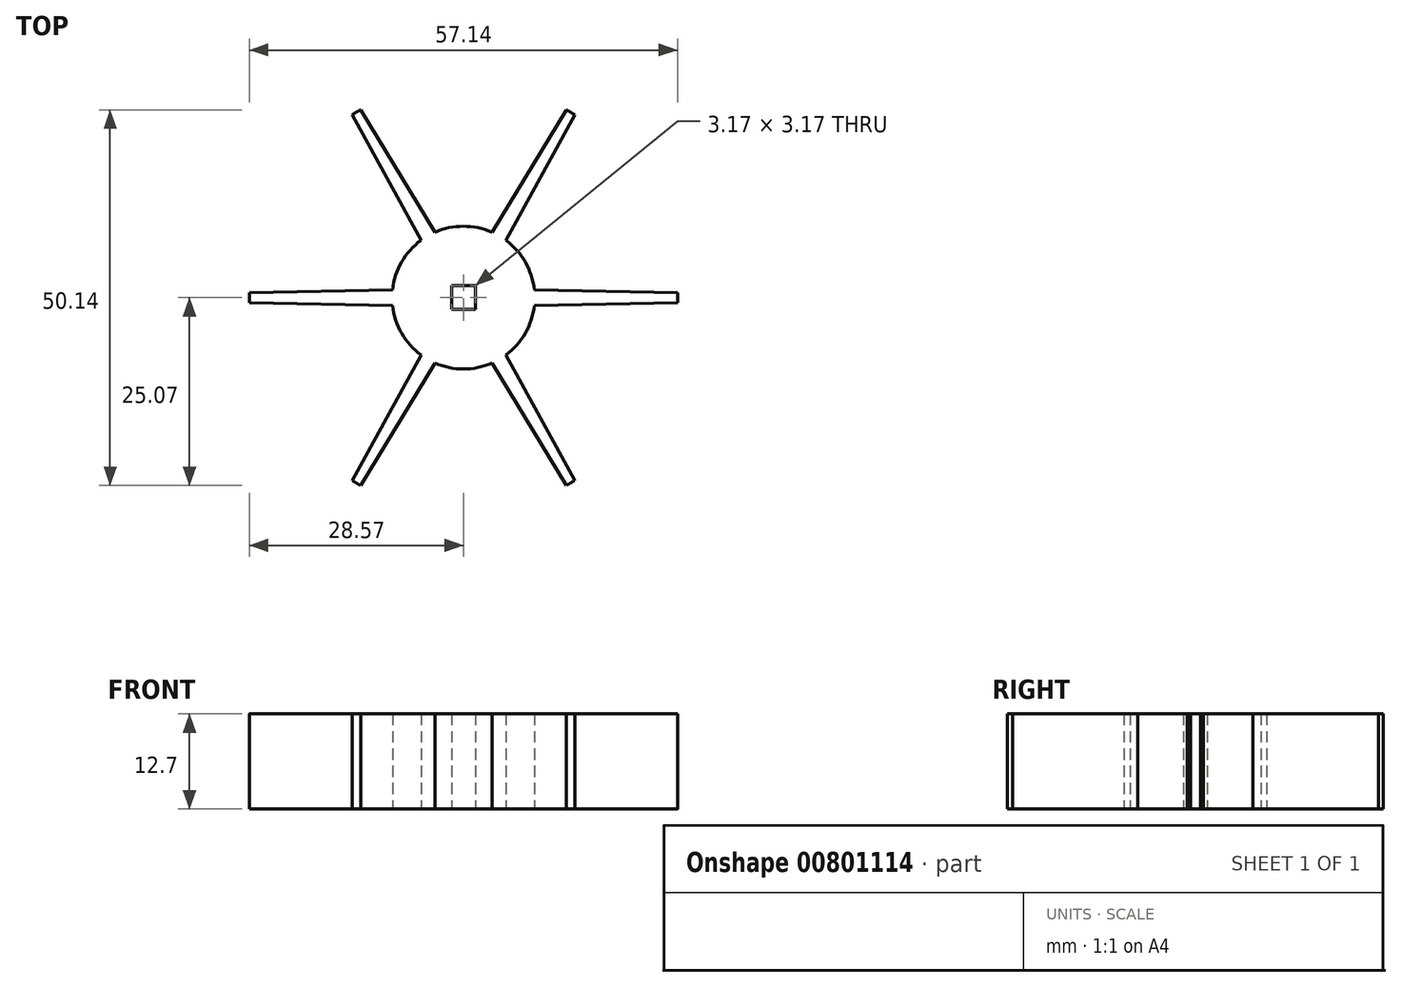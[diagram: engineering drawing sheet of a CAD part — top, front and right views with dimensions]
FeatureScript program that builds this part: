
annotation { "Feature Type Name" : "Feature", "Feature Type Description" : "" }
export const myFeature = defineFeature(function(context is Context, id is Id, definition is map)
    precondition{}
    {
        {
            var Q0;
            Q0=qCreatedBy(makeId("Top.planeOp"),FACE);
            var sketch = newSketch(context, id + "F0", { "sketchPlane" : qUnion([Q0])});
            skCircle(sketch, "E0", {"center": v(0, 0) * mm, "radius": 28.58 * mm});
            skCircle(sketch, "E1", {"center": v(0, 0) * mm, "radius": 9.53 * mm});
            skLineSegment(sketch, "E2", {"start": v(0, 0) * mm, "end": v(0, -28.58) * mm, "construction": true});
            skLineSegment(sketch, "E3", {"start": v(-3.8, -8.73) * mm, "end": v(-13.72, -25.07) * mm});
            skLineSegment(sketch, "E4.MirrorCS", {"start": v(3.81, -8.73) * mm, "end": v(13.72, -25.07) * mm});
            skLineSegment(sketch, "E5.1.1", {"start": v(9.47, -1.07) * mm, "end": v(28.57, -0.66) * mm});
            skLineSegment(sketch, "E5.1.2", {"start": v(5.66, -7.66) * mm, "end": v(14.85, -24.41) * mm});
            skLineSegment(sketch, "E5.2.1", {"start": v(5.66, 7.66) * mm, "end": v(14.85, 24.41) * mm});
            skLineSegment(sketch, "E5.2.2", {"start": v(9.47, 1.07) * mm, "end": v(28.57, 0.66) * mm});
            skLineSegment(sketch, "E5.3.1", {"start": v(-3.8, 8.73) * mm, "end": v(-13.72, 25.07) * mm});
            skLineSegment(sketch, "E5.3.2", {"start": v(3.81, 8.73) * mm, "end": v(13.72, 25.07) * mm});
            skLineSegment(sketch, "E5.4.1", {"start": v(-9.47, 1.07) * mm, "end": v(-28.57, 0.66) * mm});
            skLineSegment(sketch, "E5.4.2", {"start": v(-5.66, 7.66) * mm, "end": v(-14.85, 24.41) * mm});
            skLineSegment(sketch, "E5.5.1", {"start": v(-5.66, -7.66) * mm, "end": v(-14.85, -24.41) * mm});
            skLineSegment(sketch, "E5.5.2", {"start": v(-9.47, -1.07) * mm, "end": v(-28.57, -0.66) * mm});
            skLineSegment(sketch, "E6.bottom", {"start": v(1.59, 1.59) * mm, "end": v(-1.59, 1.59) * mm});
            skLineSegment(sketch, "E6.top", {"start": v(1.59, -1.59) * mm, "end": v(-1.59, -1.59) * mm});
            skLineSegment(sketch, "E6.left", {"start": v(1.59, 1.59) * mm, "end": v(1.59, -1.59) * mm});
            skLineSegment(sketch, "E6.right", {"start": v(-1.59, 1.59) * mm, "end": v(-1.59, -1.59) * mm});
            skSolve(sketch);
        }
        {
            var Q0;
            Q0=makeQuery(id+"F0.imprint","IMPRINT",FACE,{"disambiguationData":[TD([[makeQuery(id+"F0.imprint","IMPRINT",EDGE,{"derivedFrom":sQuery(id+"F0.wireOp",EDGE,"E6.bottom")}),-1.0]])]});
            var Q1;
            {var subQ0=sQuery(id+"F0.wireOp",EDGE,"E5.4.1");Q1=makeQuery(id+"F0.imprint","IMPRINT",FACE,{"disambiguationData":[TD([[makeQuery(id+"F0.imprint","IMPRINT",EDGE,{"derivedFrom":subQ0}),1.0]])]});}
            var Q2;
            {var subQ0=sQuery(id+"F0.wireOp",EDGE,"E5.3.1");Q2=makeQuery(id+"F0.imprint","IMPRINT",FACE,{"disambiguationData":[TD([[makeQuery(id+"F0.imprint","IMPRINT",EDGE,{"derivedFrom":subQ0}),1.0]])]});}
            var Q3;
            {var subQ0=sQuery(id+"F0.wireOp",EDGE,"E5.2.1");Q3=makeQuery(id+"F0.imprint","IMPRINT",FACE,{"disambiguationData":[TD([[makeQuery(id+"F0.imprint","IMPRINT",EDGE,{"derivedFrom":subQ0}),1.0]])]});}
            var Q4;
            {var subQ0=sQuery(id+"F0.wireOp",EDGE,"E5.1.1");Q4=makeQuery(id+"F0.imprint","IMPRINT",FACE,{"disambiguationData":[TD([[makeQuery(id+"F0.imprint","IMPRINT",EDGE,{"derivedFrom":subQ0}),1.0]])]});}
            var Q5;
            {var subQ0=sQuery(id+"F0.wireOp",EDGE,"E4.MirrorCS");Q5=makeQuery(id+"F0.imprint","IMPRINT",FACE,{"disambiguationData":[TD([[makeQuery(id+"F0.imprint","IMPRINT",EDGE,{"derivedFrom":subQ0}),1.0]])]});}
            var Q6;
            {var subQ0=sQuery(id+"F0.wireOp",EDGE,"E3");Q6=makeQuery(id+"F0.imprint","IMPRINT",FACE,{"disambiguationData":[TD([[makeQuery(id+"F0.imprint","IMPRINT",EDGE,{"derivedFrom":subQ0}),-1.0]])]});}
            extrude(context, id + "F1", {"entities" : qUnion([Q0, Q1, Q2, Q3, Q4, Q5, Q6]), "depth" : 12.7 * mm, "offsetDistance" : 25.4 * mm});
        }
    });
